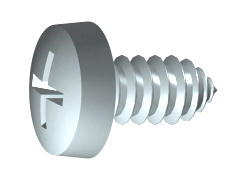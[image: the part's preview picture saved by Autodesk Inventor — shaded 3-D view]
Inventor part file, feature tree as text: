
AUTODESK INVENTOR PART (.ipt)
format: ipt  version: unknown  size: 338,944 bytes
history: native  units: mm (DEFAULTED — no unit token found)
features: other x2, plane x2, extrude x1
ambient origin geometry x8: Origin, YZ Plane, XZ Plane, XY Plane, X Axis, Y Axis, Z Axis, Center Point
feature tree (5):
  other  "Körper"
  plane  "Work Plane1"
  extrude  "Loch"  Depth=2.9mm
  other  "Schnitt"
  plane  "Work Plane3"
